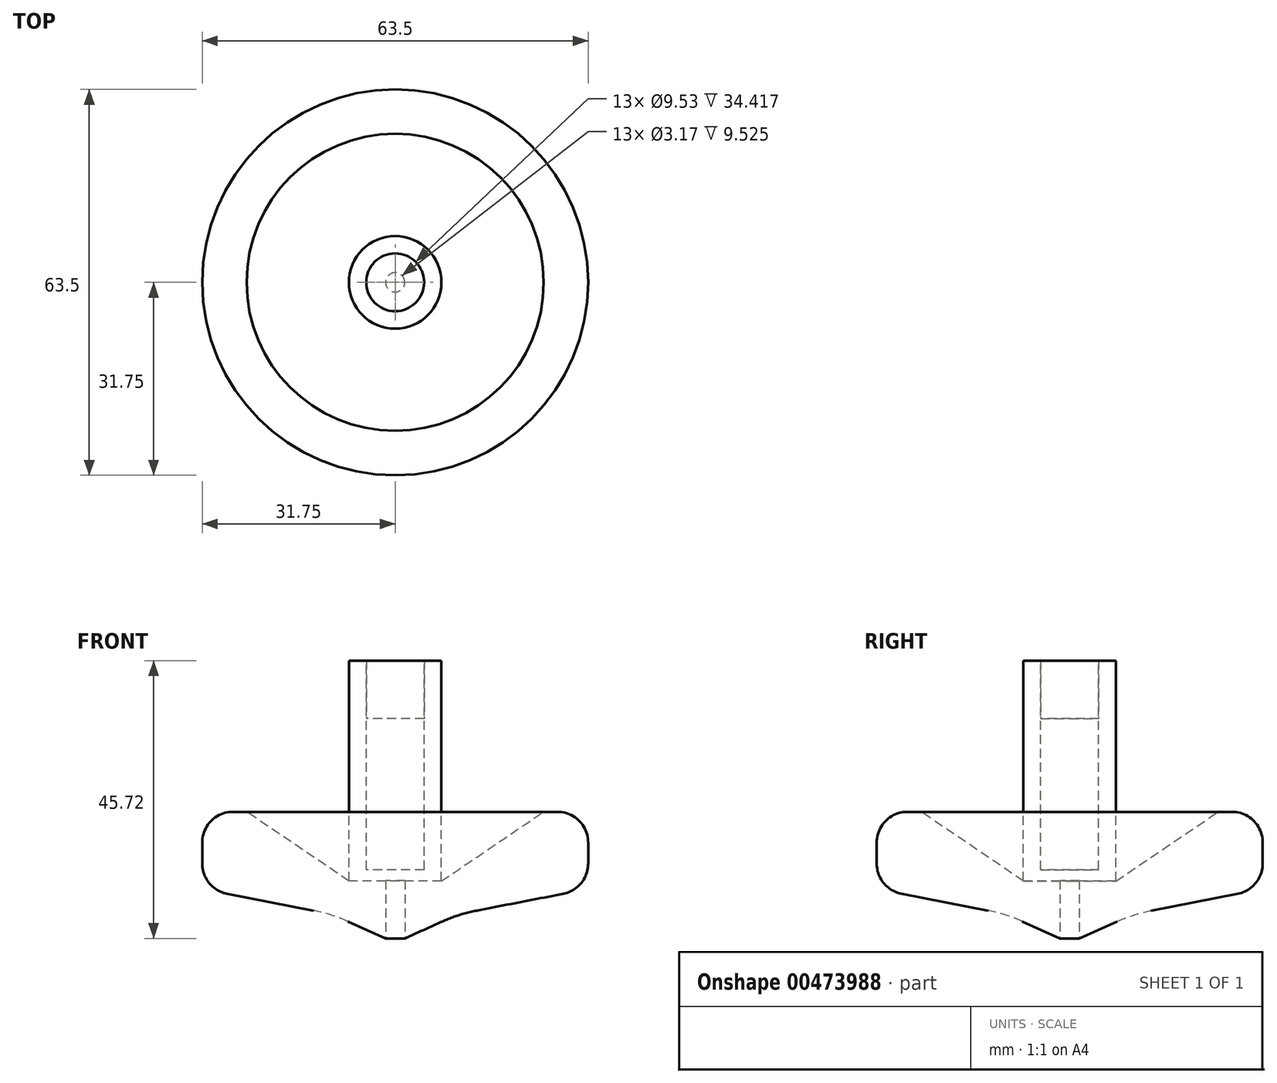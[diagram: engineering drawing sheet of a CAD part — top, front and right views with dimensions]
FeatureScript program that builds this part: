
annotation { "Feature Type Name" : "Feature", "Feature Type Description" : "" }
export const myFeature = defineFeature(function(context is Context, id is Id, definition is map)
    precondition{}
    {
        {
            var Q0;
            Q0=qCreatedBy(makeId("Front.planeOp"),FACE);
            var sketch = newSketch(context, id + "F0", { "sketchPlane" : qUnion([Q0])});
            skLineSegment(sketch, "E0", {"start": v(31.75, 8.13) * mm, "end": v(31.75, 20.83) * mm});
            skLineSegment(sketch, "E1", {"start": v(31.75, 20.83) * mm, "end": v(24.44, 20.83) * mm});
            skLineSegment(sketch, "E2", {"start": v(24.44, 20.83) * mm, "end": v(7.62, 9.44) * mm});
            skLineSegment(sketch, "E3", {"start": v(7.62, 9.44) * mm, "end": v(7.62, 45.72) * mm});
            skLineSegment(sketch, "E4", {"start": v(7.62, 45.72) * mm, "end": v(0, 45.72) * mm});
            skLineSegment(sketch, "E5", {"start": v(0, 45.72) * mm, "end": v(0, 0) * mm});
            skLineSegment(sketch, "E6", {"start": v(10.5, 4.02) * mm, "end": v(31.75, 8.13) * mm});
            skLineSegment(sketch, "E7", {"start": v(0, 0) * mm, "end": v(1.59, 0) * mm});
            skLineSegment(sketch, "E8", {"start": v(1.59, 0) * mm, "end": v(10.5, 4.02) * mm});
            skSolve(sketch);
        }
        {
            var Q0;
            Q0=qSketchRegion(id+"F0",true);
            var Q1;
            Q1=sQuery(id+"F0.wireOp",EDGE,"E5");
            revolve(context, id + "F1", {"entities" : qUnion([Q0]), "axis" : qUnion([Q1]), "revolveType" : RevolveType.FULL});
        }
        {
            var Q0;
            Q0=makeQuery(id+"F1.opRevolve","SWEPT_FACE",FACE,{"disambiguationData":[OSD([sQuery(id+"F0.wireOp",EDGE,"E0")])]});
            fillet(context, id + "F2", {"entities" : qUnion([Q0]), "radius" : 5.08 * mm, "tangentPropagation" : true, "allowEdgeOverflow" : false});
        }
        {
            var Q0;
            Q0=makeQuery(id+"F1.opRevolve","SWEPT_EDGE",EDGE,{"disambiguationData":[OSD([sQuery(id+"F0.wireOp",EDGE,"E6"),sQuery(id+"F0.wireOp",EDGE,"E8")])]});
            fillet(context, id + "F3", {"entities" : qUnion([Q0]), "radius" : 25.4 * mm, "tangentPropagation" : true, "allowEdgeOverflow" : false});
        }
        {
            var Q0;
            Q0=makeQuery(id+"F1.opRevolve","SWEPT_FACE",FACE,{"disambiguationData":[OSD([sQuery(id+"F0.wireOp",EDGE,"E4")])]});
            var sketch = newSketch(context, id + "F4", { "sketchPlane" : qUnion([Q0])});
            skCircle(sketch, "E9", {"center": v(0, 0) * mm, "radius": 4.76 * mm});
            skSolve(sketch);
        }
        {
            var Q0;
            Q0=qSketchRegion(id+"F4",true);
            extrude(context, id + "F5", {"entities" : qUnion([Q0]), "operationType" : NewBodyOperationType.REMOVE, "oppositeDirection" : true, "depth" : 9.52 * mm});
        }
        {
            var Q0;
            Q0=qCreatedBy(makeId("Top.planeOp"),FACE);
            var sketch = newSketch(context, id + "F6", { "sketchPlane" : qUnion([Q0])});
            skCircle(sketch, "E10", {"center": v(0, 0) * mm, "radius": 1.59 * mm});
            skSolve(sketch);
        }
        {
            var Q0;
            Q0=qSketchRegion(id+"F6",true);
            extrude(context, id + "F7", {"entities" : qUnion([Q0]), "operationType" : NewBodyOperationType.REMOVE, "depth" : 9.52 * mm});
        }
        {
            var Q0;
            Q0=makeQuery(id+"F5.boolean.opBoolean","COPY",FACE,{"derivedFrom":makeQuery(id+"F5.opExtrude","CAP_FACE",FACE,{"disambiguationData":[OSD([sQuery(id+"F4.wireOp",EDGE,"E9")])],"isStart":false})});
            extrude(context, id + "F8", {"entities" : qUnion([Q0]), "depth" : 9.52 * mm});
        }
        {
            var Q0;
            Q0=makeQuery(id+"F5.boolean.opBoolean","COPY",FACE,{"derivedFrom":makeQuery(id+"F5.opExtrude","CAP_FACE",FACE,{"disambiguationData":[OSD([sQuery(id+"F4.wireOp",EDGE,"E9")])],"isStart":false})});
            extrude(context, id + "F9", {"entities" : qUnion([Q0]), "operationType" : NewBodyOperationType.REMOVE, "oppositeDirection" : true, "depth" : 24.9 * mm});
        }
    });
